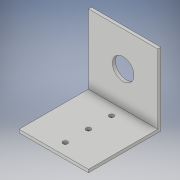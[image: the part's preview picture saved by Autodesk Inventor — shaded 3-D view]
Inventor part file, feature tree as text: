
AUTODESK INVENTOR PART (.ipt)
format: ipt  version: 2019 (Build 230136000, 136)  size: 141,824 bytes
history: native  units: mm
features: sketch x6, extrude x3, hole x2, other x1
ambient origin geometry x8: Origin, YZ Plane, XZ Plane, XY Plane, X Axis, Y Axis, Z Axis, Center Point
bodies: Body1 (feature_tree)
feature tree (12):
  other  "ソリッド1"
  sketch  "スケッチ1"
  sketch  "スケッチ2"
  extrude  "押し出し1"  Depth=45.0mm
  hole  "穴1"  [1 undecoded]
  extrude  "押し出し2"  Depth=2.0mm TaperAngle=0.0deg
  extrude  "押し出し3"  Depth=8.0mm
  hole  "穴2"  [1 undecoded]
  sketch  "スケッチ3"
  sketch  "スケッチ4"
  sketch  "スケッチ5"
  sketch  "スケッチ6"
note: 2 required parameter values undecoded (feature->parameter linkage not recoverable at this tier; creation-order binding heuristic only, values carry confidence <= 0.55)
